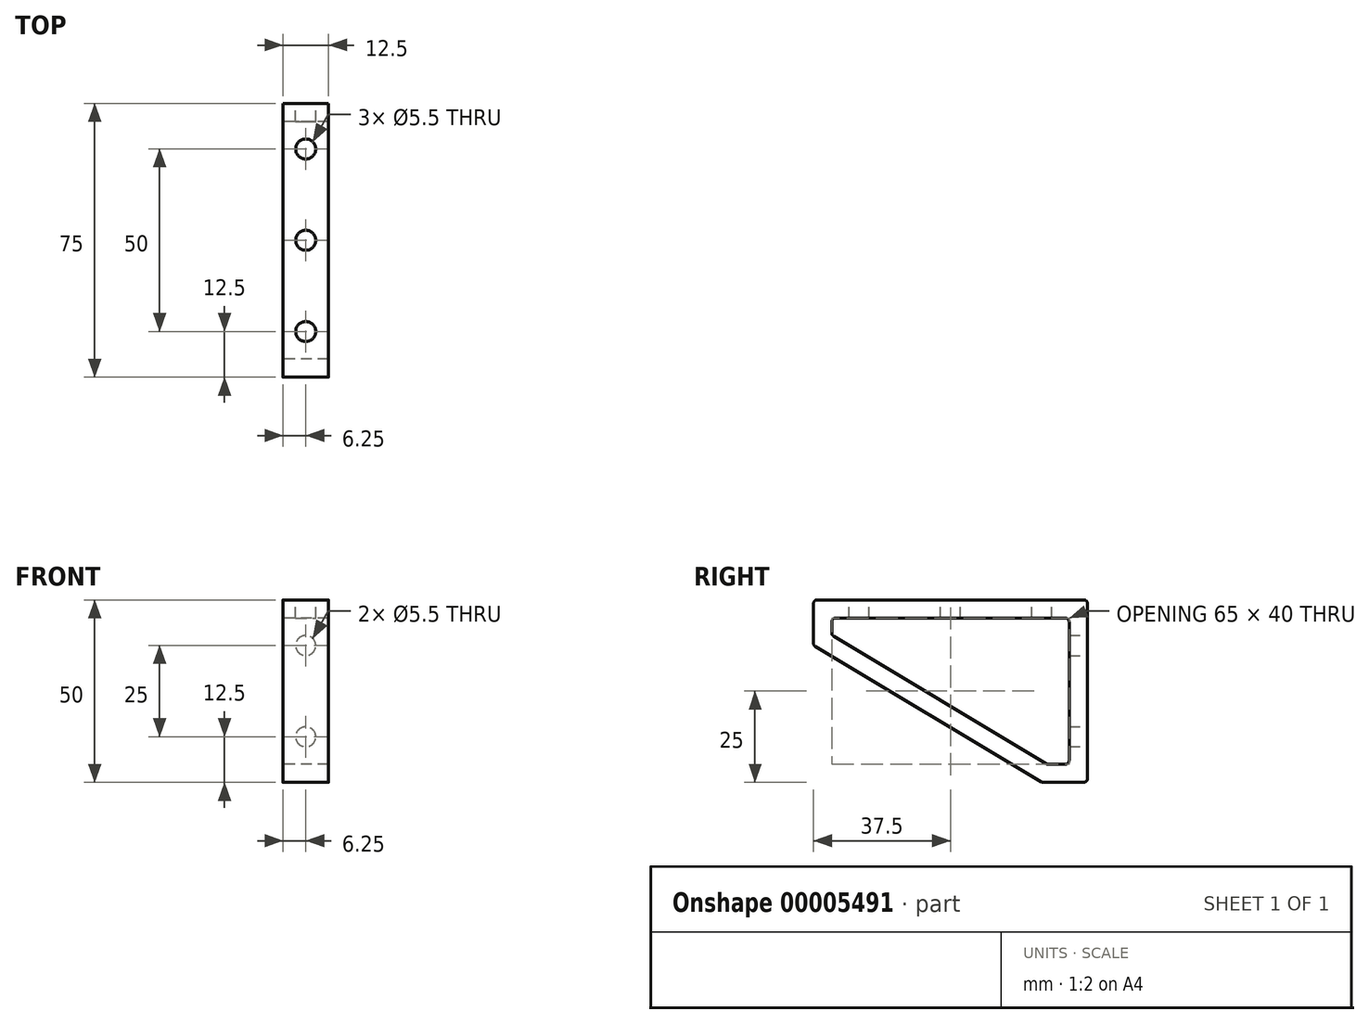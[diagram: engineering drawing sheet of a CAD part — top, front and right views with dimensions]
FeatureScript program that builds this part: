
annotation { "Feature Type Name" : "Feature", "Feature Type Description" : "" }
export const myFeature = defineFeature(function(context is Context, id is Id, definition is map)
    precondition{}
    {
        {
            var Q0;
            Q0=qCreatedBy(makeId("Right.planeOp"),FACE);
            var sketch = newSketch(context, id + "F0", { "sketchPlane" : qUnion([Q0])});
            skLineSegment(sketch, "E0", {"start": v(0, 0) * mm, "end": v(0, -50) * mm});
            skLineSegment(sketch, "E1", {"start": v(0, 0) * mm, "end": v(-75, 0) * mm});
            skLineSegment(sketch, "E2", {"start": v(-75, 0) * mm, "end": v(-75, -12.5) * mm});
            skLineSegment(sketch, "E3", {"start": v(-75, -12.5) * mm, "end": v(-12.5, -50) * mm});
            skLineSegment(sketch, "E4", {"start": v(0, -50) * mm, "end": v(-12.5, -50) * mm});
            skSolve(sketch);
        }
        {
            var Q0;
            Q0=makeQuery(id+"F0.imprint","IMPRINT",FACE,{"disambiguationData":[TD([[makeQuery(id+"F0.imprint","IMPRINT",EDGE,{"derivedFrom":sQuery(id+"F0.wireOp",EDGE,"E0")}),-1.0]])]});
            extrude(context, id + "F1", {"entities" : qUnion([Q0]), "depth" : 12.5 * mm});
        }
        {
            var Q0;
            Q0=makeQuery(id+"F1.opExtrude","CAP_FACE",FACE,{"disambiguationData":[OSD([sQuery(id+"F0.wireOp",EDGE,"E0"),sQuery(id+"F0.wireOp",EDGE,"E1"),sQuery(id+"F0.wireOp",EDGE,"33bea93b-b1e7-484a-a300-cced40a43aed")])],"isStart":true});
            var Q1;
            Q1=makeQuery(id+"F1.opExtrude","CAP_FACE",FACE,{"disambiguationData":[OSD([sQuery(id+"F0.wireOp",EDGE,"E0"),sQuery(id+"F0.wireOp",EDGE,"E1"),sQuery(id+"F0.wireOp",EDGE,"33bea93b-b1e7-484a-a300-cced40a43aed")])],"isStart":false});
            shell(context, id + "F2", {"entities" : qUnion([Q0, Q1]), "thickness" : 5 * mm});
        }
        {
            var Q0;
            Q0=makeQuery(id+"F1.opExtrude","SWEPT_FACE",FACE,{"disambiguationData":[OSD([sQuery(id+"F0.wireOp",EDGE,"E0")])]});
            var sketch = newSketch(context, id + "F3", { "sketchPlane" : qUnion([Q0])});
            skCircle(sketch, "E5", {"center": v(-6.25, -12.5) * mm, "radius": 2.75 * mm});
            skPoint(sketch, "E6", {"position": v(-6.25, 0) * mm});
            skCircle(sketch, "E7.0.1.0", {"center": v(-6.25, -37.5) * mm, "radius": 2.75 * mm});
            skCircle(sketch, "E7.0.2.0", {"center": v(-6.25, -62.5) * mm, "radius": 2.75 * mm});
            skCircle(sketch, "E7.0.3.0", {"center": v(-6.25, -87.5) * mm, "radius": 2.75 * mm});
            skCircle(sketch, "E7.0.4.0", {"center": v(-6.25, -112.5) * mm, "radius": 2.75 * mm});
            skLineSegment(sketch, "E7.direction1", {"start": v(-6.25, -12.5) * mm, "end": v(18.75, -12.5) * mm, "construction": true});
            skLineSegment(sketch, "E7.direction2", {"start": v(-6.25, -12.5) * mm, "end": v(-6.25, -37.5) * mm, "construction": true});
            skSolve(sketch);
        }
        {
            var Q0;
            Q0 = qSketchRegion(id + "F3", true);
            var Q1;
            Q1=makeQuery(id+"F2.opShell","OFFSET_FACE",FACE,{"disambiguationData":[OSD([sQuery(id+"F0.wireOp",EDGE,"E0")])]});
            extrude(context, id + "F4", {"entities" : qUnion([Q0]), "operationType" : NewBodyOperationType.REMOVE, "endBound" : BoundingType.UP_TO_SURFACE, "oppositeDirection" : true, "endBoundEntityFace" : qUnion([Q1]), "depth" : 25 * mm});
        }
        {
            var Q0;
            Q0=makeQuery(id+"F1.opExtrude","SWEPT_FACE",FACE,{"disambiguationData":[OSD([sQuery(id+"F0.wireOp",EDGE,"E1")])]});
            var sketch = newSketch(context, id + "F5", { "sketchPlane" : qUnion([Q0])});
            skPoint(sketch, "E8", {"position": v(6.25, 0) * mm});
            skCircle(sketch, "E9", {"center": v(6.25, -12.5) * mm, "radius": 2.75 * mm});
            skCircle(sketch, "E10.0.1.0", {"center": v(6.25, -37.5) * mm, "radius": 2.75 * mm});
            skCircle(sketch, "E10.0.2.0", {"center": v(6.25, -62.5) * mm, "radius": 2.75 * mm});
            skLineSegment(sketch, "E10.direction1", {"start": v(6.25, -12.5) * mm, "end": v(35, -12.5) * mm, "construction": true});
            skLineSegment(sketch, "E10.direction2", {"start": v(6.25, -12.5) * mm, "end": v(6.25, -37.5) * mm, "construction": true});
            skCircle(sketch, "E11.0.0.3", {"center": v(6.25, -87.5) * mm, "radius": 2.75 * mm});
            skCircle(sketch, "E11.0.0.4", {"center": v(6.25, -112.5) * mm, "radius": 2.75 * mm});
            skSolve(sketch);
        }
        {
            var Q0;
            {Q0=qUnion([makeQuery(id+"F5.imprint","IMPRINT",FACE,{"disambiguationData":[TD([[makeQuery(id+"F5.imprint","IMPRINT",EDGE,{"derivedFrom":sQuery(id+"F5.wireOp",EDGE,"E11.0.0.3")}),1.0]])]}),makeQuery(id+"F5.imprint","IMPRINT",FACE,{"disambiguationData":[TD([[makeQuery(id+"F5.imprint","IMPRINT",EDGE,{"derivedFrom":sQuery(id+"F5.wireOp",EDGE,"E11.0.0.4")}),1.0]])]}),makeQuery(id+"F5.imprint","IMPRINT",FACE,{"disambiguationData":[TD([[makeQuery(id+"F5.imprint","IMPRINT",EDGE,{"derivedFrom":sQuery(id+"F5.wireOp",EDGE,"E9")}),1.0]])]}),makeQuery(id+"F5.imprint","IMPRINT",FACE,{"disambiguationData":[TD([[makeQuery(id+"F5.imprint","IMPRINT",EDGE,{"derivedFrom":sQuery(id+"F5.wireOp",EDGE,"E10.0.1.0")}),1.0]])]}),makeQuery(id+"F5.imprint","IMPRINT",FACE,{"disambiguationData":[TD([[makeQuery(id+"F5.imprint","IMPRINT",EDGE,{"derivedFrom":sQuery(id+"F5.wireOp",EDGE,"E10.0.2.0")}),1.0]])]})]);}
            var Q1;
            Q1=makeQuery(id+"F2.opShell","OFFSET_FACE",FACE,{"disambiguationData":[OSD([sQuery(id+"F0.wireOp",EDGE,"E1")])]});
            extrude(context, id + "F6", {"entities" : qUnion([Q0]), "operationType" : NewBodyOperationType.REMOVE, "endBound" : BoundingType.UP_TO_SURFACE, "oppositeDirection" : true, "endBoundEntityFace" : qUnion([Q1]), "depth" : 25 * mm});
        }
        {
            var Q0;
            Q0=makeQuery(id+"F2.opShell","OFFSET_EDGE",EDGE,{"disambiguationData":[OSD([sQuery(id+"F0.wireOp",EDGE,"E0"),sQuery(id+"F0.wireOp",EDGE,"E1")])]});
            var Q1;
            Q1=makeQuery(id+"F2.opShell","OFFSET_EDGE",EDGE,{"disambiguationData":[OSD([sQuery(id+"F0.wireOp",EDGE,"E1"),sQuery(id+"F0.wireOp",EDGE,"E2")])]});
            var Q2;
            Q2=makeQuery(id+"F2.opShell","OFFSET_EDGE",EDGE,{"disambiguationData":[OSD([sQuery(id+"F0.wireOp",EDGE,"E2"),sQuery(id+"F0.wireOp",EDGE,"E3")])]});
            var Q3;
            Q3=makeQuery(id+"F2.opShell","OFFSET_EDGE",EDGE,{"disambiguationData":[OSD([sQuery(id+"F0.wireOp",EDGE,"E3"),sQuery(id+"F0.wireOp",EDGE,"E4")])]});
            var Q4;
            Q4=makeQuery(id+"F2.opShell","OFFSET_EDGE",EDGE,{"disambiguationData":[OSD([sQuery(id+"F0.wireOp",EDGE,"E0"),sQuery(id+"F0.wireOp",EDGE,"E4")])]});
            var Q5;
            Q5=makeQuery(id+"F1.opExtrude","SWEPT_EDGE",EDGE,{"disambiguationData":[OSD([sQuery(id+"F0.wireOp",EDGE,"E0"),sQuery(id+"F0.wireOp",EDGE,"E4")])]});
            var Q6;
            Q6=makeQuery(id+"F1.opExtrude","SWEPT_EDGE",EDGE,{"disambiguationData":[OSD([sQuery(id+"F0.wireOp",EDGE,"E3"),sQuery(id+"F0.wireOp",EDGE,"E4")])]});
            var Q7;
            Q7=makeQuery(id+"F1.opExtrude","SWEPT_EDGE",EDGE,{"disambiguationData":[OSD([sQuery(id+"F0.wireOp",EDGE,"E2"),sQuery(id+"F0.wireOp",EDGE,"E3")])]});
            var Q8;
            Q8=makeQuery(id+"F1.opExtrude","SWEPT_EDGE",EDGE,{"disambiguationData":[OSD([sQuery(id+"F0.wireOp",EDGE,"E0"),sQuery(id+"F0.wireOp",EDGE,"E1")])]});
            var Q9;
            Q9=makeQuery(id+"F1.opExtrude","SWEPT_EDGE",EDGE,{"disambiguationData":[OSD([sQuery(id+"F0.wireOp",EDGE,"E1"),sQuery(id+"F0.wireOp",EDGE,"E2")])]});
            fillet(context, id + "F7", {"entities" : qUnion([Q0, Q1, Q2, Q3, Q4, Q5, Q6, Q7, Q8, Q9]), "radius" : 1 * mm, "tangentPropagation" : true, "allowEdgeOverflow" : false});
        }
    });
